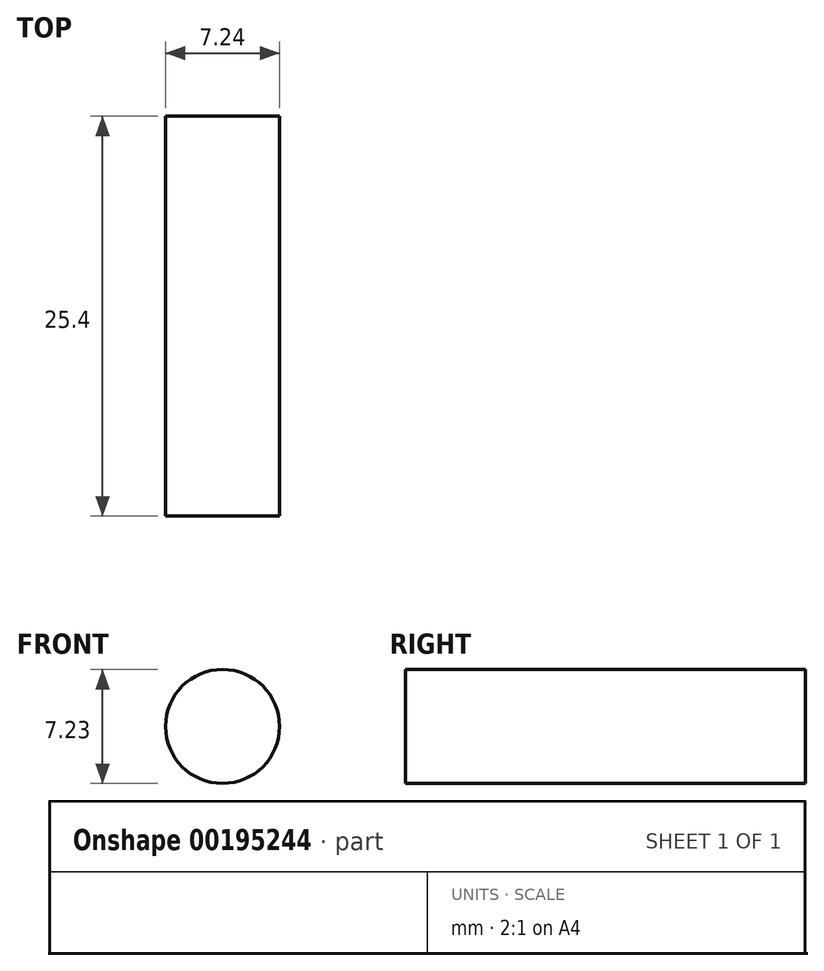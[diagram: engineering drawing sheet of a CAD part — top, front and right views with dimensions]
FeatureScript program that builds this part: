
annotation { "Feature Type Name" : "Feature", "Feature Type Description" : "" }
export const myFeature = defineFeature(function(context is Context, id is Id, definition is map)
    precondition{}
    {
        {
            var Q0;
            Q0=qCreatedBy(makeId("Front.planeOp"),FACE);
            var sketch = newSketch(context, id + "F0", { "sketchPlane" : qUnion([Q0])});
            skCircle(sketch, "E0", {"center": v(-45.97, 34.84) * mm, "radius": 3.62 * mm});
            skSolve(sketch);
        }
        {
            var Q0;
            Q0 = qSketchRegion(id + "F0", true);
            extrude(context, id + "F1", {"entities" : qUnion([Q0]), "depth" : 25.4 * mm});
        }
    });
